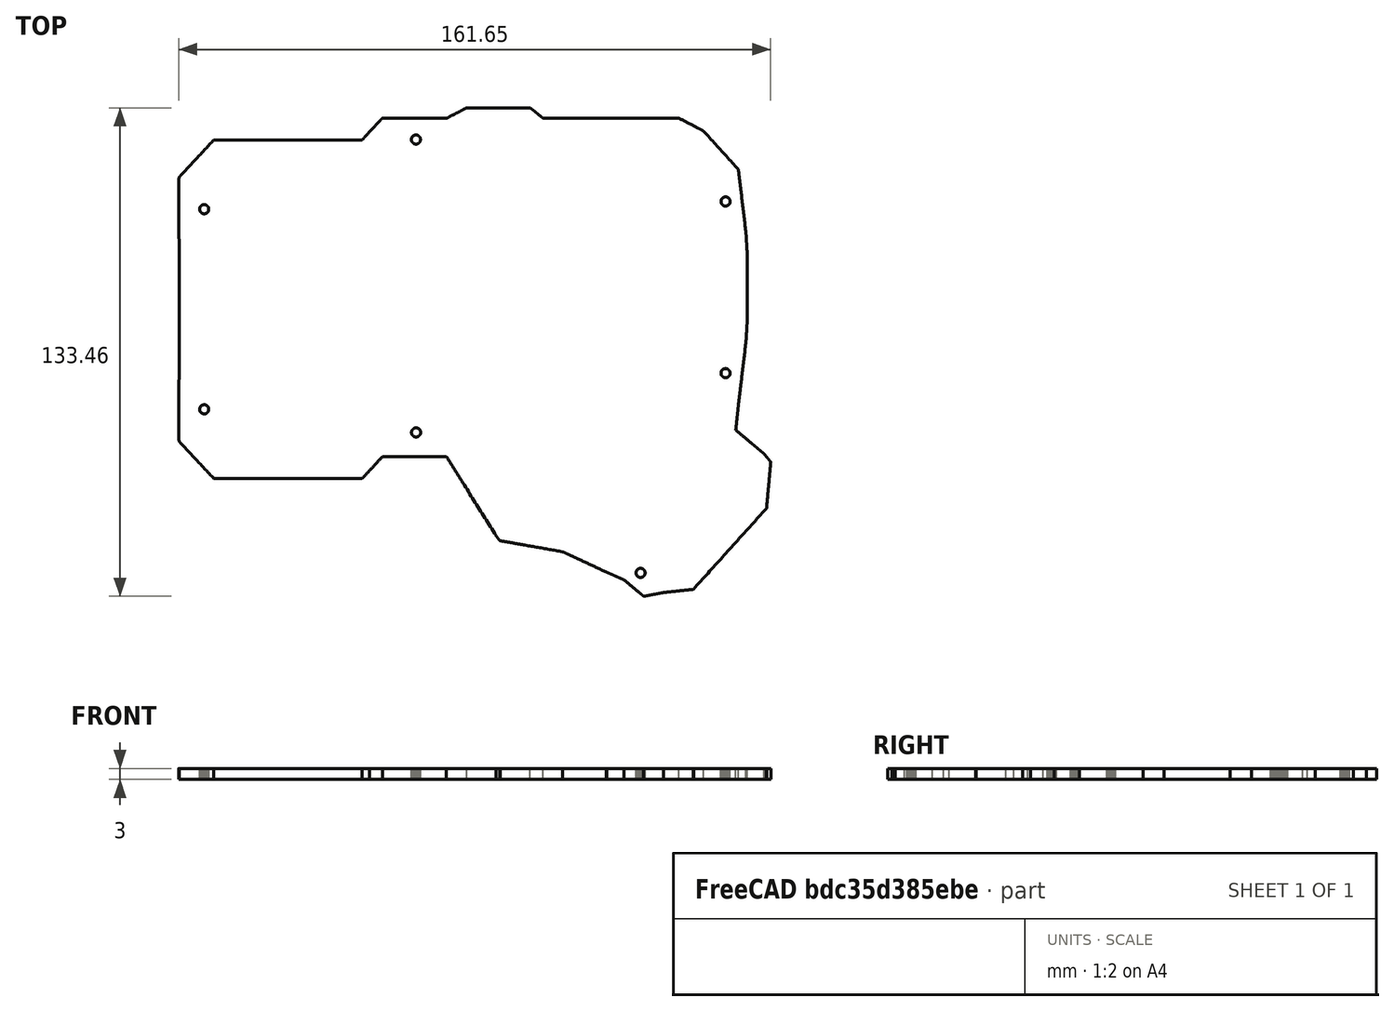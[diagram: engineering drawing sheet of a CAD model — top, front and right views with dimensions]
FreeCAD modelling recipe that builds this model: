
FCSTD DOCUMENT  (FreeCAD 0.19R24267 +99 (Git))
Label: DM_plate
License: All rights reserved
LicenseURL: http://en.wikipedia.org/wiki/All_rights_reserved
objects: Part::Feature×8, Part::MultiFuse×1, Part::Cut×1, Part::Extrusion×1
note: 11 computed .brp shape members not serialized (recipe doc carries the construction recipe); baked Part::Feature solids carry a one-line shape summary decoded from their .brp

FEATURE [Part::Feature] Path
  shape: bbox 161.7 x 133.5 x 2e-07 mm, 1 faces, 0 solids (baked)
FEATURE [Part::Feature] Path001
  shape: bbox 2.5 x 2.502 x 2e-07 mm, 1 faces, 0 solids (baked)
FEATURE [Part::Feature] Path002
  shape: bbox 2.502 x 2.5 x 2e-07 mm, 1 faces, 0 solids (baked)
FEATURE [Part::Feature] Path003
  shape: bbox 2.5 x 2.498 x 2e-07 mm, 1 faces, 0 solids (baked)
FEATURE [Part::Feature] Path004
  shape: bbox 2.5 x 2.5 x 2e-07 mm, 1 faces, 0 solids (baked)
FEATURE [Part::Feature] Path005
  shape: bbox 2.5 x 2.5 x 2e-07 mm, 1 faces, 0 solids (baked)
FEATURE [Part::Feature] Path006
  shape: bbox 2.5 x 2.498 x 2e-07 mm, 1 faces, 0 solids (baked)
FEATURE [Part::Feature] Path008
  shape: bbox 2.502 x 2.498 x 2e-07 mm, 1 faces, 0 solids (baked)
FEATURE [Part::MultiFuse] Fusion
  Shapes = -> [Path001,Path002,Path003,Path004,Path005,Path006,Path008]
FEATURE [Part::Cut] Cut
  Base = -> Path
  Tool = -> Fusion
FEATURE [Part::Extrusion] Extrude
  Base = -> Cut
  Dir = (0,0,1)
  DirMode = 0
  FaceMakerClass = Part::FaceMakerBullseye
  LengthFwd = 3
  LengthRev = 0
  Solid = false
  Symmetric = false
